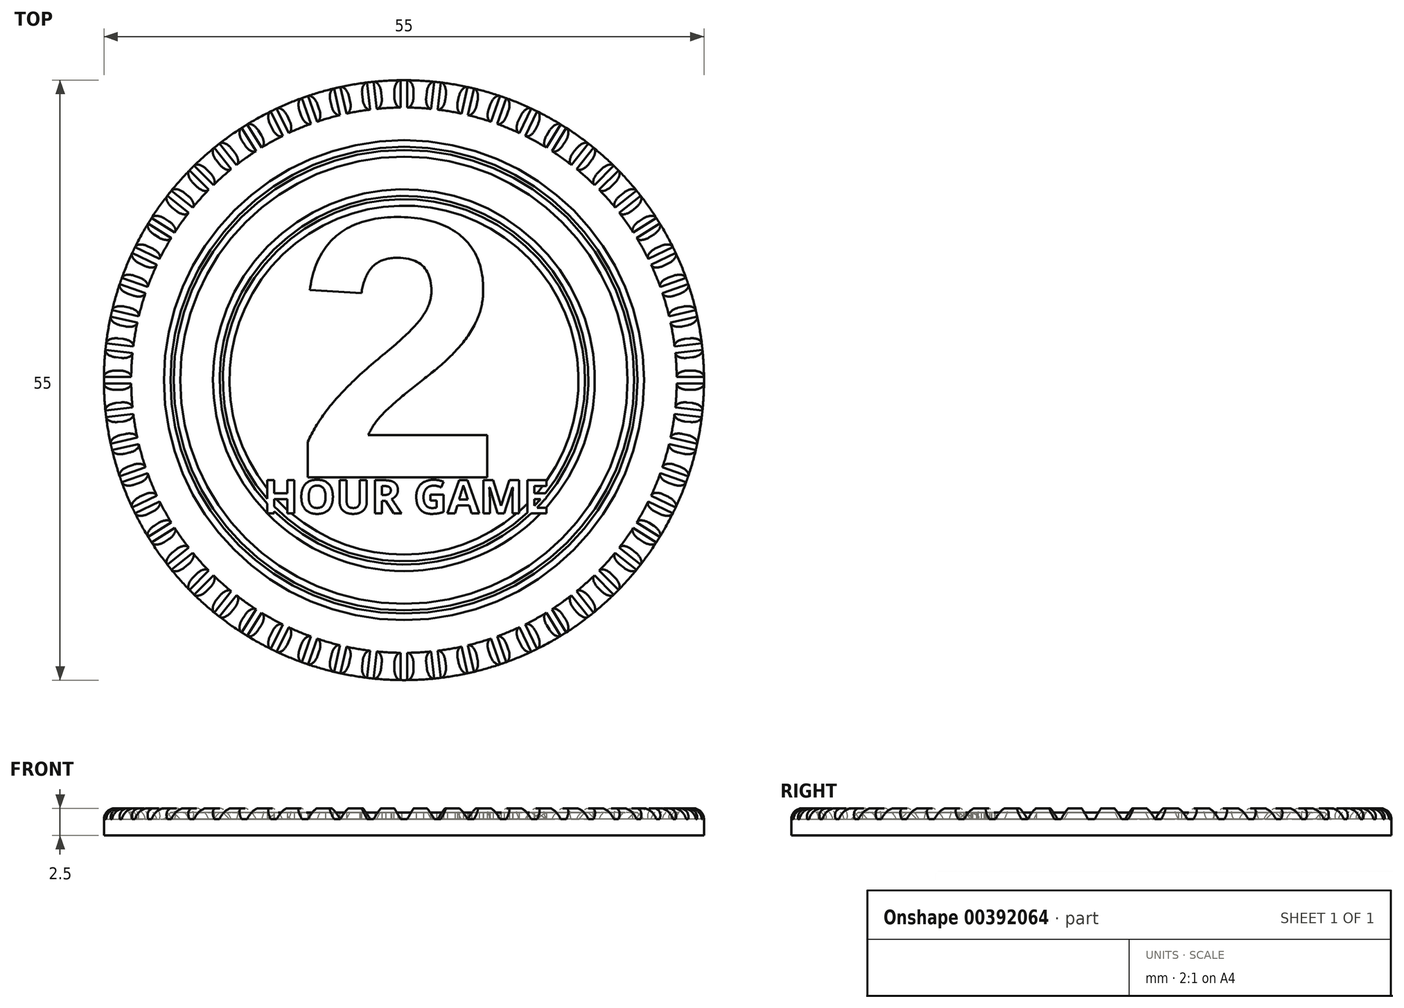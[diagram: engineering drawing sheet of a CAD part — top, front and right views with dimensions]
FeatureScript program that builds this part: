
annotation { "Feature Type Name" : "Feature", "Feature Type Description" : "" }
export const myFeature = defineFeature(function(context is Context, id is Id, definition is map)
    precondition{}
    {
        {
            var Q0;
            Q0=qCreatedBy(makeId("Top.planeOp"),FACE);
            var sketch = newSketch(context, id + "F0", { "sketchPlane" : qUnion([Q0])});
            skCircle(sketch, "E0", {"center": v(0, 0) * mm, "radius": 27.5 * mm});
            skSolve(sketch);
        }
        {
            var Q0;
            Q0=qSketchRegion(id+"F0",true);
            extrude(context, id + "F1", {"entities" : qUnion([Q0]), "depth" : 2.5 * mm});
        }
        {
            var Q0;
            Q0=makeQuery(id+"F1.opExtrude","CAP_FACE",FACE,{"disambiguationData":[OSD([sQuery(id+"F0.wireOp",EDGE,"E0")])],"isStart":false});
            var sketch = newSketch(context, id + "F2", { "sketchPlane" : qUnion([Q0])});
            skCircle(sketch, "E1.0", {"center": v(0, 0) * mm, "radius": 25 * mm});
            skSolve(sketch);
        }
        {
            var Q0;
            Q0=qSketchRegion(id+"F2",true);
            extrude(context, id + "F3", {"entities" : qUnion([Q0]), "operationType" : NewBodyOperationType.REMOVE, "oppositeDirection" : true, "depth" : 1 * mm});
        }
        {
            var Q0;
            Q0=makeQuery(id+"F1.opExtrude","CAP_FACE",FACE,{"disambiguationData":[OSD([sQuery(id+"F0.wireOp",EDGE,"E0")])],"isStart":false});
            fillet(context, id + "F4", {"entities" : qUnion([Q0]), "radius" : 1 * mm, "tangentPropagation" : true, "allowEdgeOverflow" : false});
        }
        {
            var Q0;
            Q0=qCreatedBy(makeId("Right.planeOp"),FACE);
            var sketch = newSketch(context, id + "F5", { "sketchPlane" : qUnion([Q0])});
            skLineSegment(sketch, "E2", {"start": v(0, 0) * mm, "end": v(0, 4.13) * mm, "construction": true});
            skLineSegment(sketch, "E3", {"start": v(0, 1.5) * mm, "end": v(-0.3, 1.5) * mm});
            skLineSegment(sketch, "E4", {"start": v(-0.3, 1.5) * mm, "end": v(-0.88, 2.5) * mm});
            skLineSegment(sketch, "E5", {"start": v(-0.88, 2.5) * mm, "end": v(0, 2.5) * mm});
            skLineSegment(sketch, "E6.MirrorCS", {"start": v(0, 1.5) * mm, "end": v(0.3, 1.5) * mm});
            skLineSegment(sketch, "E7.MirrorCS", {"start": v(0.88, 2.5) * mm, "end": v(0, 2.5) * mm});
            skLineSegment(sketch, "E8.MirrorCS", {"start": v(0.3, 1.5) * mm, "end": v(0.88, 2.5) * mm});
            skSolve(sketch);
        }
        {
            var Q0;
            Q0=qSketchRegion(id+"F5",true);
            extrude(context, id + "F6", {"entities" : qUnion([Q0]), "endBound" : BoundingType.THROUGH_ALL, "oppositeDirection" : true, "depth" : 25 * mm});
        }
        {
            var Q0;
            Q0=qCreatedBy(makeId("Front.planeOp"),FACE);
            var sketch = newSketch(context, id + "F7", { "sketchPlane" : qUnion([Q0])});
            skLineSegment(sketch, "E9", {"start": v(0, 0) * mm, "end": v(0, 9.54) * mm});
            skSolve(sketch);
        }
        {
            var Q0;
            Q0=makeQuery(id+"F6.opExtrude","SWEPT_BODY",BODY,{"disambiguationData":[OSD([sQuery(id+"F5.wireOp",EDGE,"E3"),sQuery(id+"F5.wireOp",EDGE,"E4"),sQuery(id+"F5.wireOp",EDGE,"E5"),sQuery(id+"F5.wireOp",EDGE,"E6.MirrorCS"),sQuery(id+"F5.wireOp",EDGE,"E7.MirrorCS"),sQuery(id+"F5.wireOp",EDGE,"E8.MirrorCS")])]});
            var Q1;
            Q1=sQuery(id+"F7.wireOp",EDGE,"E9");
            circularPattern(context, id + "F8", {"operationType" : NewBodyOperationType.REMOVE, "entities" : qUnion([Q0]), "axis" : qUnion([Q1]), "angle" : 360 * degree, "instanceCount" : 56, "equalSpace" : true, "computeTransformsWithoutBuiltin" : true});
        }
        {
            var Q0;
            {var subQ0=makeQuery(id+"F6.opExtrude","SWEPT_FACE",FACE,{"disambiguationData":[OSD([sQuery(id+"F5.wireOp",EDGE,"E3"),sQuery(id+"F5.wireOp",EDGE,"E6.MirrorCS")])]});Q0=makeQuery(id+"F8.boolean.opBoolean","MERGE",FACE,{"derivedFrom":[makeQuery(id+"F3.boolean.opBoolean","COPY",FACE,{"derivedFrom":makeQuery(id+"F3.opExtrude","CAP_FACE",FACE,{"disambiguationData":[OSD([sQuery(id+"F2.wireOp",EDGE,"E1.0")])],"isStart":false})}),subQ0,makeQuery(id+"F8.opPattern","COPY",FACE,{"derivedFrom":subQ0,"instanceName":"1"}),makeQuery(id+"F8.opPattern","COPY",FACE,{"derivedFrom":subQ0,"instanceName":"2"}),makeQuery(id+"F8.opPattern","COPY",FACE,{"derivedFrom":subQ0,"instanceName":"3"}),makeQuery(id+"F8.opPattern","COPY",FACE,{"derivedFrom":subQ0,"instanceName":"4"}),makeQuery(id+"F8.opPattern","COPY",FACE,{"derivedFrom":subQ0,"instanceName":"5"}),makeQuery(id+"F8.opPattern","COPY",FACE,{"derivedFrom":subQ0,"instanceName":"6"}),makeQuery(id+"F8.opPattern","COPY",FACE,{"derivedFrom":subQ0,"instanceName":"7"}),makeQuery(id+"F8.opPattern","COPY",FACE,{"derivedFrom":subQ0,"instanceName":"8"}),makeQuery(id+"F8.opPattern","COPY",FACE,{"derivedFrom":subQ0,"instanceName":"9"}),makeQuery(id+"F8.opPattern","COPY",FACE,{"derivedFrom":subQ0,"instanceName":"10"}),makeQuery(id+"F8.opPattern","COPY",FACE,{"derivedFrom":subQ0,"instanceName":"11"}),makeQuery(id+"F8.opPattern","COPY",FACE,{"derivedFrom":subQ0,"instanceName":"12"}),makeQuery(id+"F8.opPattern","COPY",FACE,{"derivedFrom":subQ0,"instanceName":"13"}),makeQuery(id+"F8.opPattern","COPY",FACE,{"derivedFrom":subQ0,"instanceName":"14"}),makeQuery(id+"F8.opPattern","COPY",FACE,{"derivedFrom":subQ0,"instanceName":"15"}),makeQuery(id+"F8.opPattern","COPY",FACE,{"derivedFrom":subQ0,"instanceName":"16"}),makeQuery(id+"F8.opPattern","COPY",FACE,{"derivedFrom":subQ0,"instanceName":"17"}),makeQuery(id+"F8.opPattern","COPY",FACE,{"derivedFrom":subQ0,"instanceName":"18"}),makeQuery(id+"F8.opPattern","COPY",FACE,{"derivedFrom":subQ0,"instanceName":"19"}),makeQuery(id+"F8.opPattern","COPY",FACE,{"derivedFrom":subQ0,"instanceName":"20"}),makeQuery(id+"F8.opPattern","COPY",FACE,{"derivedFrom":subQ0,"instanceName":"21"}),makeQuery(id+"F8.opPattern","COPY",FACE,{"derivedFrom":subQ0,"instanceName":"22"}),makeQuery(id+"F8.opPattern","COPY",FACE,{"derivedFrom":subQ0,"instanceName":"23"}),makeQuery(id+"F8.opPattern","COPY",FACE,{"derivedFrom":subQ0,"instanceName":"24"}),makeQuery(id+"F8.opPattern","COPY",FACE,{"derivedFrom":subQ0,"instanceName":"25"}),makeQuery(id+"F8.opPattern","COPY",FACE,{"derivedFrom":subQ0,"instanceName":"26"}),makeQuery(id+"F8.opPattern","COPY",FACE,{"derivedFrom":subQ0,"instanceName":"27"}),makeQuery(id+"F8.opPattern","COPY",FACE,{"derivedFrom":subQ0,"instanceName":"28"}),makeQuery(id+"F8.opPattern","COPY",FACE,{"derivedFrom":subQ0,"instanceName":"29"}),makeQuery(id+"F8.opPattern","COPY",FACE,{"derivedFrom":subQ0,"instanceName":"30"}),makeQuery(id+"F8.opPattern","COPY",FACE,{"derivedFrom":subQ0,"instanceName":"31"}),makeQuery(id+"F8.opPattern","COPY",FACE,{"derivedFrom":subQ0,"instanceName":"32"}),makeQuery(id+"F8.opPattern","COPY",FACE,{"derivedFrom":subQ0,"instanceName":"33"}),makeQuery(id+"F8.opPattern","COPY",FACE,{"derivedFrom":subQ0,"instanceName":"34"}),makeQuery(id+"F8.opPattern","COPY",FACE,{"derivedFrom":subQ0,"instanceName":"35"}),makeQuery(id+"F8.opPattern","COPY",FACE,{"derivedFrom":subQ0,"instanceName":"36"}),makeQuery(id+"F8.opPattern","COPY",FACE,{"derivedFrom":subQ0,"instanceName":"37"}),makeQuery(id+"F8.opPattern","COPY",FACE,{"derivedFrom":subQ0,"instanceName":"38"}),makeQuery(id+"F8.opPattern","COPY",FACE,{"derivedFrom":subQ0,"instanceName":"39"}),makeQuery(id+"F8.opPattern","COPY",FACE,{"derivedFrom":subQ0,"instanceName":"40"}),makeQuery(id+"F8.opPattern","COPY",FACE,{"derivedFrom":subQ0,"instanceName":"41"}),makeQuery(id+"F8.opPattern","COPY",FACE,{"derivedFrom":subQ0,"instanceName":"42"}),makeQuery(id+"F8.opPattern","COPY",FACE,{"derivedFrom":subQ0,"instanceName":"43"}),makeQuery(id+"F8.opPattern","COPY",FACE,{"derivedFrom":subQ0,"instanceName":"44"}),makeQuery(id+"F8.opPattern","COPY",FACE,{"derivedFrom":subQ0,"instanceName":"45"}),makeQuery(id+"F8.opPattern","COPY",FACE,{"derivedFrom":subQ0,"instanceName":"46"}),makeQuery(id+"F8.opPattern","COPY",FACE,{"derivedFrom":subQ0,"instanceName":"47"}),makeQuery(id+"F8.opPattern","COPY",FACE,{"derivedFrom":subQ0,"instanceName":"48"}),makeQuery(id+"F8.opPattern","COPY",FACE,{"derivedFrom":subQ0,"instanceName":"49"}),makeQuery(id+"F8.opPattern","COPY",FACE,{"derivedFrom":subQ0,"instanceName":"50"}),makeQuery(id+"F8.opPattern","COPY",FACE,{"derivedFrom":subQ0,"instanceName":"51"}),makeQuery(id+"F8.opPattern","COPY",FACE,{"derivedFrom":subQ0,"instanceName":"52"}),makeQuery(id+"F8.opPattern","COPY",FACE,{"derivedFrom":subQ0,"instanceName":"53"}),makeQuery(id+"F8.opPattern","COPY",FACE,{"derivedFrom":subQ0,"instanceName":"54"}),makeQuery(id+"F8.opPattern","COPY",FACE,{"derivedFrom":subQ0,"instanceName":"55"})]});}
            var sketch = newSketch(context, id + "F9", { "sketchPlane" : qUnion([Q0])});
            skText(sketch, "E10", { "text": "2", "fontName": "Arimo-Bold.ttf"});
            const initialGuessF9  = {"E10": [-0.01, -0.0089, 1, 0, 0.0246]};
            skSetInitialGuess(sketch, initialGuessF9);
            skSolve(sketch);
        }
        {
            var Q0;
            Q0=qSketchRegion(id+"F9",true);
            extrude(context, id + "F10", {"entities" : qUnion([Q0]), "operationType" : NewBodyOperationType.ADD, "depth" : 0.6 * mm});
        }
        {
            var Q0;
            {var subQ0=makeQuery(id+"F6.opExtrude","SWEPT_FACE",FACE,{"disambiguationData":[OSD([sQuery(id+"F5.wireOp",EDGE,"E3"),sQuery(id+"F5.wireOp",EDGE,"E6.MirrorCS")])]});Q0=makeQuery(id+"F8.boolean.opBoolean","MERGE",FACE,{"derivedFrom":[makeQuery(id+"F3.boolean.opBoolean","COPY",FACE,{"derivedFrom":makeQuery(id+"F3.opExtrude","CAP_FACE",FACE,{"disambiguationData":[OSD([sQuery(id+"F2.wireOp",EDGE,"E1.0")])],"isStart":false})}),subQ0,makeQuery(id+"F8.opPattern","COPY",FACE,{"derivedFrom":subQ0,"instanceName":"1"}),makeQuery(id+"F8.opPattern","COPY",FACE,{"derivedFrom":subQ0,"instanceName":"2"}),makeQuery(id+"F8.opPattern","COPY",FACE,{"derivedFrom":subQ0,"instanceName":"3"}),makeQuery(id+"F8.opPattern","COPY",FACE,{"derivedFrom":subQ0,"instanceName":"4"}),makeQuery(id+"F8.opPattern","COPY",FACE,{"derivedFrom":subQ0,"instanceName":"5"}),makeQuery(id+"F8.opPattern","COPY",FACE,{"derivedFrom":subQ0,"instanceName":"6"}),makeQuery(id+"F8.opPattern","COPY",FACE,{"derivedFrom":subQ0,"instanceName":"7"}),makeQuery(id+"F8.opPattern","COPY",FACE,{"derivedFrom":subQ0,"instanceName":"8"}),makeQuery(id+"F8.opPattern","COPY",FACE,{"derivedFrom":subQ0,"instanceName":"9"}),makeQuery(id+"F8.opPattern","COPY",FACE,{"derivedFrom":subQ0,"instanceName":"10"}),makeQuery(id+"F8.opPattern","COPY",FACE,{"derivedFrom":subQ0,"instanceName":"11"}),makeQuery(id+"F8.opPattern","COPY",FACE,{"derivedFrom":subQ0,"instanceName":"12"}),makeQuery(id+"F8.opPattern","COPY",FACE,{"derivedFrom":subQ0,"instanceName":"13"}),makeQuery(id+"F8.opPattern","COPY",FACE,{"derivedFrom":subQ0,"instanceName":"14"}),makeQuery(id+"F8.opPattern","COPY",FACE,{"derivedFrom":subQ0,"instanceName":"15"}),makeQuery(id+"F8.opPattern","COPY",FACE,{"derivedFrom":subQ0,"instanceName":"16"}),makeQuery(id+"F8.opPattern","COPY",FACE,{"derivedFrom":subQ0,"instanceName":"17"}),makeQuery(id+"F8.opPattern","COPY",FACE,{"derivedFrom":subQ0,"instanceName":"18"}),makeQuery(id+"F8.opPattern","COPY",FACE,{"derivedFrom":subQ0,"instanceName":"19"}),makeQuery(id+"F8.opPattern","COPY",FACE,{"derivedFrom":subQ0,"instanceName":"20"}),makeQuery(id+"F8.opPattern","COPY",FACE,{"derivedFrom":subQ0,"instanceName":"21"}),makeQuery(id+"F8.opPattern","COPY",FACE,{"derivedFrom":subQ0,"instanceName":"22"}),makeQuery(id+"F8.opPattern","COPY",FACE,{"derivedFrom":subQ0,"instanceName":"23"}),makeQuery(id+"F8.opPattern","COPY",FACE,{"derivedFrom":subQ0,"instanceName":"24"}),makeQuery(id+"F8.opPattern","COPY",FACE,{"derivedFrom":subQ0,"instanceName":"25"}),makeQuery(id+"F8.opPattern","COPY",FACE,{"derivedFrom":subQ0,"instanceName":"26"}),makeQuery(id+"F8.opPattern","COPY",FACE,{"derivedFrom":subQ0,"instanceName":"27"}),makeQuery(id+"F8.opPattern","COPY",FACE,{"derivedFrom":subQ0,"instanceName":"28"}),makeQuery(id+"F8.opPattern","COPY",FACE,{"derivedFrom":subQ0,"instanceName":"29"}),makeQuery(id+"F8.opPattern","COPY",FACE,{"derivedFrom":subQ0,"instanceName":"30"}),makeQuery(id+"F8.opPattern","COPY",FACE,{"derivedFrom":subQ0,"instanceName":"31"}),makeQuery(id+"F8.opPattern","COPY",FACE,{"derivedFrom":subQ0,"instanceName":"32"}),makeQuery(id+"F8.opPattern","COPY",FACE,{"derivedFrom":subQ0,"instanceName":"33"}),makeQuery(id+"F8.opPattern","COPY",FACE,{"derivedFrom":subQ0,"instanceName":"34"}),makeQuery(id+"F8.opPattern","COPY",FACE,{"derivedFrom":subQ0,"instanceName":"35"}),makeQuery(id+"F8.opPattern","COPY",FACE,{"derivedFrom":subQ0,"instanceName":"36"}),makeQuery(id+"F8.opPattern","COPY",FACE,{"derivedFrom":subQ0,"instanceName":"37"}),makeQuery(id+"F8.opPattern","COPY",FACE,{"derivedFrom":subQ0,"instanceName":"38"}),makeQuery(id+"F8.opPattern","COPY",FACE,{"derivedFrom":subQ0,"instanceName":"39"}),makeQuery(id+"F8.opPattern","COPY",FACE,{"derivedFrom":subQ0,"instanceName":"40"}),makeQuery(id+"F8.opPattern","COPY",FACE,{"derivedFrom":subQ0,"instanceName":"41"}),makeQuery(id+"F8.opPattern","COPY",FACE,{"derivedFrom":subQ0,"instanceName":"42"}),makeQuery(id+"F8.opPattern","COPY",FACE,{"derivedFrom":subQ0,"instanceName":"43"}),makeQuery(id+"F8.opPattern","COPY",FACE,{"derivedFrom":subQ0,"instanceName":"44"}),makeQuery(id+"F8.opPattern","COPY",FACE,{"derivedFrom":subQ0,"instanceName":"45"}),makeQuery(id+"F8.opPattern","COPY",FACE,{"derivedFrom":subQ0,"instanceName":"46"}),makeQuery(id+"F8.opPattern","COPY",FACE,{"derivedFrom":subQ0,"instanceName":"47"}),makeQuery(id+"F8.opPattern","COPY",FACE,{"derivedFrom":subQ0,"instanceName":"48"}),makeQuery(id+"F8.opPattern","COPY",FACE,{"derivedFrom":subQ0,"instanceName":"49"}),makeQuery(id+"F8.opPattern","COPY",FACE,{"derivedFrom":subQ0,"instanceName":"50"}),makeQuery(id+"F8.opPattern","COPY",FACE,{"derivedFrom":subQ0,"instanceName":"51"}),makeQuery(id+"F8.opPattern","COPY",FACE,{"derivedFrom":subQ0,"instanceName":"52"}),makeQuery(id+"F8.opPattern","COPY",FACE,{"derivedFrom":subQ0,"instanceName":"53"}),makeQuery(id+"F8.opPattern","COPY",FACE,{"derivedFrom":subQ0,"instanceName":"54"}),makeQuery(id+"F8.opPattern","COPY",FACE,{"derivedFrom":subQ0,"instanceName":"55"})]});}
            var sketch = newSketch(context, id + "F11", { "sketchPlane" : qUnion([Q0])});
            skText(sketch, "E11", { "text": "HOUR GAME", "fontName": "OpenSans-Bold.ttf"});
            const initialGuessF11  = {"E11": [-0.01292, -0.01222, 1, 0, 0.00307]};
            skSetInitialGuess(sketch, initialGuessF11);
            skSolve(sketch);
        }
        {
            var Q0;
            Q0=qSketchRegion(id+"F11",true);
            extrude(context, id + "F12", {"entities" : qUnion([Q0]), "operationType" : NewBodyOperationType.ADD, "depth" : 0.6 * mm});
        }
        {
            var Q0;
            {var subQ2=sQuery(id+"F0.wireOp",EDGE,"E0");var subQ3=sQuery(id+"F2.wireOp",EDGE,"E1.0");var subQ4=makeQuery(id+"F6.opExtrude","SWEPT_FACE",FACE,{"disambiguationData":[OSD([sQuery(id+"F5.wireOp",EDGE,"E3"),sQuery(id+"F5.wireOp",EDGE,"E6.MirrorCS")])]});Q0=makeQuery(id+"F12.boolean.opBoolean","SPLIT",FACE,{"disambiguationData":[TD([makeQuery(id+"F1.opExtrude","SWEPT_FACE",FACE,{"disambiguationData":[OSD([subQ2])]})])],"derivedFrom":makeQuery(id+"F8.boolean.opBoolean","MERGE",FACE,{"derivedFrom":[makeQuery(id+"F3.boolean.opBoolean","COPY",FACE,{"derivedFrom":makeQuery(id+"F3.opExtrude","CAP_FACE",FACE,{"disambiguationData":[OSD([subQ3])],"isStart":false})}),subQ4,makeQuery(id+"F8.opPattern","COPY",FACE,{"derivedFrom":subQ4,"instanceName":"1"}),makeQuery(id+"F8.opPattern","COPY",FACE,{"derivedFrom":subQ4,"instanceName":"2"}),makeQuery(id+"F8.opPattern","COPY",FACE,{"derivedFrom":subQ4,"instanceName":"3"}),makeQuery(id+"F8.opPattern","COPY",FACE,{"derivedFrom":subQ4,"instanceName":"4"}),makeQuery(id+"F8.opPattern","COPY",FACE,{"derivedFrom":subQ4,"instanceName":"5"}),makeQuery(id+"F8.opPattern","COPY",FACE,{"derivedFrom":subQ4,"instanceName":"6"}),makeQuery(id+"F8.opPattern","COPY",FACE,{"derivedFrom":subQ4,"instanceName":"7"}),makeQuery(id+"F8.opPattern","COPY",FACE,{"derivedFrom":subQ4,"instanceName":"8"}),makeQuery(id+"F8.opPattern","COPY",FACE,{"derivedFrom":subQ4,"instanceName":"9"}),makeQuery(id+"F8.opPattern","COPY",FACE,{"derivedFrom":subQ4,"instanceName":"10"}),makeQuery(id+"F8.opPattern","COPY",FACE,{"derivedFrom":subQ4,"instanceName":"11"}),makeQuery(id+"F8.opPattern","COPY",FACE,{"derivedFrom":subQ4,"instanceName":"12"}),makeQuery(id+"F8.opPattern","COPY",FACE,{"derivedFrom":subQ4,"instanceName":"13"}),makeQuery(id+"F8.opPattern","COPY",FACE,{"derivedFrom":subQ4,"instanceName":"14"}),makeQuery(id+"F8.opPattern","COPY",FACE,{"derivedFrom":subQ4,"instanceName":"15"}),makeQuery(id+"F8.opPattern","COPY",FACE,{"derivedFrom":subQ4,"instanceName":"16"}),makeQuery(id+"F8.opPattern","COPY",FACE,{"derivedFrom":subQ4,"instanceName":"17"}),makeQuery(id+"F8.opPattern","COPY",FACE,{"derivedFrom":subQ4,"instanceName":"18"}),makeQuery(id+"F8.opPattern","COPY",FACE,{"derivedFrom":subQ4,"instanceName":"19"}),makeQuery(id+"F8.opPattern","COPY",FACE,{"derivedFrom":subQ4,"instanceName":"20"}),makeQuery(id+"F8.opPattern","COPY",FACE,{"derivedFrom":subQ4,"instanceName":"21"}),makeQuery(id+"F8.opPattern","COPY",FACE,{"derivedFrom":subQ4,"instanceName":"22"}),makeQuery(id+"F8.opPattern","COPY",FACE,{"derivedFrom":subQ4,"instanceName":"23"}),makeQuery(id+"F8.opPattern","COPY",FACE,{"derivedFrom":subQ4,"instanceName":"24"}),makeQuery(id+"F8.opPattern","COPY",FACE,{"derivedFrom":subQ4,"instanceName":"25"}),makeQuery(id+"F8.opPattern","COPY",FACE,{"derivedFrom":subQ4,"instanceName":"26"}),makeQuery(id+"F8.opPattern","COPY",FACE,{"derivedFrom":subQ4,"instanceName":"27"}),makeQuery(id+"F8.opPattern","COPY",FACE,{"derivedFrom":subQ4,"instanceName":"28"}),makeQuery(id+"F8.opPattern","COPY",FACE,{"derivedFrom":subQ4,"instanceName":"29"}),makeQuery(id+"F8.opPattern","COPY",FACE,{"derivedFrom":subQ4,"instanceName":"30"}),makeQuery(id+"F8.opPattern","COPY",FACE,{"derivedFrom":subQ4,"instanceName":"31"}),makeQuery(id+"F8.opPattern","COPY",FACE,{"derivedFrom":subQ4,"instanceName":"32"}),makeQuery(id+"F8.opPattern","COPY",FACE,{"derivedFrom":subQ4,"instanceName":"33"}),makeQuery(id+"F8.opPattern","COPY",FACE,{"derivedFrom":subQ4,"instanceName":"34"}),makeQuery(id+"F8.opPattern","COPY",FACE,{"derivedFrom":subQ4,"instanceName":"35"}),makeQuery(id+"F8.opPattern","COPY",FACE,{"derivedFrom":subQ4,"instanceName":"36"}),makeQuery(id+"F8.opPattern","COPY",FACE,{"derivedFrom":subQ4,"instanceName":"37"}),makeQuery(id+"F8.opPattern","COPY",FACE,{"derivedFrom":subQ4,"instanceName":"38"}),makeQuery(id+"F8.opPattern","COPY",FACE,{"derivedFrom":subQ4,"instanceName":"39"}),makeQuery(id+"F8.opPattern","COPY",FACE,{"derivedFrom":subQ4,"instanceName":"40"}),makeQuery(id+"F8.opPattern","COPY",FACE,{"derivedFrom":subQ4,"instanceName":"41"}),makeQuery(id+"F8.opPattern","COPY",FACE,{"derivedFrom":subQ4,"instanceName":"42"}),makeQuery(id+"F8.opPattern","COPY",FACE,{"derivedFrom":subQ4,"instanceName":"43"}),makeQuery(id+"F8.opPattern","COPY",FACE,{"derivedFrom":subQ4,"instanceName":"44"}),makeQuery(id+"F8.opPattern","COPY",FACE,{"derivedFrom":subQ4,"instanceName":"45"}),makeQuery(id+"F8.opPattern","COPY",FACE,{"derivedFrom":subQ4,"instanceName":"46"}),makeQuery(id+"F8.opPattern","COPY",FACE,{"derivedFrom":subQ4,"instanceName":"47"}),makeQuery(id+"F8.opPattern","COPY",FACE,{"derivedFrom":subQ4,"instanceName":"48"}),makeQuery(id+"F8.opPattern","COPY",FACE,{"derivedFrom":subQ4,"instanceName":"49"}),makeQuery(id+"F8.opPattern","COPY",FACE,{"derivedFrom":subQ4,"instanceName":"50"}),makeQuery(id+"F8.opPattern","COPY",FACE,{"derivedFrom":subQ4,"instanceName":"51"}),makeQuery(id+"F8.opPattern","COPY",FACE,{"derivedFrom":subQ4,"instanceName":"52"}),makeQuery(id+"F8.opPattern","COPY",FACE,{"derivedFrom":subQ4,"instanceName":"53"}),makeQuery(id+"F8.opPattern","COPY",FACE,{"derivedFrom":subQ4,"instanceName":"54"}),makeQuery(id+"F8.opPattern","COPY",FACE,{"derivedFrom":subQ4,"instanceName":"55"})]})});}
            var sketch = newSketch(context, id + "F13", { "sketchPlane" : qUnion([Q0])});
            skCircle(sketch, "E12", {"center": v(0, 0) * mm, "radius": 16 * mm});
            skCircle(sketch, "E13.0", {"center": v(0, 0) * mm, "radius": 17.5 * mm});
            skSolve(sketch);
        }
        {
            var Q0;
            Q0 = qSketchRegion(id + "F13", true);
            extrude(context, id + "F14", {"entities" : qUnion([Q0]), "operationType" : NewBodyOperationType.ADD, "depth" : 0.6 * mm, "hasDraft" : true, "draftAngle" : 45 * degree, "draftPullDirection" : true});
        }
        {
            var Q0;
            {var subQ71=sQuery(id+"F0.wireOp",EDGE,"E0");var subQ76=sQuery(id+"F2.wireOp",EDGE,"E1.0");var subQ96=makeQuery(id+"F1.opExtrude","SWEPT_FACE",FACE,{"disambiguationData":[OSD([subQ71])]});var subQ140=makeQuery(id+"F6.opExtrude","SWEPT_FACE",FACE,{"disambiguationData":[OSD([sQuery(id+"F5.wireOp",EDGE,"E3"),sQuery(id+"F5.wireOp",EDGE,"E6.MirrorCS")])]});Q0=makeQuery(id+"F14.boolean.opBoolean","SPLIT",FACE,{"disambiguationData":[TD([subQ96])],"derivedFrom":makeQuery(id+"F12.boolean.opBoolean","SPLIT",FACE,{"disambiguationData":[TD([subQ96])],"derivedFrom":makeQuery(id+"F8.boolean.opBoolean","MERGE",FACE,{"derivedFrom":[makeQuery(id+"F3.boolean.opBoolean","COPY",FACE,{"derivedFrom":makeQuery(id+"F3.opExtrude","CAP_FACE",FACE,{"disambiguationData":[OSD([subQ76])],"isStart":false})}),subQ140,makeQuery(id+"F8.opPattern","COPY",FACE,{"derivedFrom":subQ140,"instanceName":"1"}),makeQuery(id+"F8.opPattern","COPY",FACE,{"derivedFrom":subQ140,"instanceName":"2"}),makeQuery(id+"F8.opPattern","COPY",FACE,{"derivedFrom":subQ140,"instanceName":"3"}),makeQuery(id+"F8.opPattern","COPY",FACE,{"derivedFrom":subQ140,"instanceName":"4"}),makeQuery(id+"F8.opPattern","COPY",FACE,{"derivedFrom":subQ140,"instanceName":"5"}),makeQuery(id+"F8.opPattern","COPY",FACE,{"derivedFrom":subQ140,"instanceName":"6"}),makeQuery(id+"F8.opPattern","COPY",FACE,{"derivedFrom":subQ140,"instanceName":"7"}),makeQuery(id+"F8.opPattern","COPY",FACE,{"derivedFrom":subQ140,"instanceName":"8"}),makeQuery(id+"F8.opPattern","COPY",FACE,{"derivedFrom":subQ140,"instanceName":"9"}),makeQuery(id+"F8.opPattern","COPY",FACE,{"derivedFrom":subQ140,"instanceName":"10"}),makeQuery(id+"F8.opPattern","COPY",FACE,{"derivedFrom":subQ140,"instanceName":"11"}),makeQuery(id+"F8.opPattern","COPY",FACE,{"derivedFrom":subQ140,"instanceName":"12"}),makeQuery(id+"F8.opPattern","COPY",FACE,{"derivedFrom":subQ140,"instanceName":"13"}),makeQuery(id+"F8.opPattern","COPY",FACE,{"derivedFrom":subQ140,"instanceName":"14"}),makeQuery(id+"F8.opPattern","COPY",FACE,{"derivedFrom":subQ140,"instanceName":"15"}),makeQuery(id+"F8.opPattern","COPY",FACE,{"derivedFrom":subQ140,"instanceName":"16"}),makeQuery(id+"F8.opPattern","COPY",FACE,{"derivedFrom":subQ140,"instanceName":"17"}),makeQuery(id+"F8.opPattern","COPY",FACE,{"derivedFrom":subQ140,"instanceName":"18"}),makeQuery(id+"F8.opPattern","COPY",FACE,{"derivedFrom":subQ140,"instanceName":"19"}),makeQuery(id+"F8.opPattern","COPY",FACE,{"derivedFrom":subQ140,"instanceName":"20"}),makeQuery(id+"F8.opPattern","COPY",FACE,{"derivedFrom":subQ140,"instanceName":"21"}),makeQuery(id+"F8.opPattern","COPY",FACE,{"derivedFrom":subQ140,"instanceName":"22"}),makeQuery(id+"F8.opPattern","COPY",FACE,{"derivedFrom":subQ140,"instanceName":"23"}),makeQuery(id+"F8.opPattern","COPY",FACE,{"derivedFrom":subQ140,"instanceName":"24"}),makeQuery(id+"F8.opPattern","COPY",FACE,{"derivedFrom":subQ140,"instanceName":"25"}),makeQuery(id+"F8.opPattern","COPY",FACE,{"derivedFrom":subQ140,"instanceName":"26"}),makeQuery(id+"F8.opPattern","COPY",FACE,{"derivedFrom":subQ140,"instanceName":"27"}),makeQuery(id+"F8.opPattern","COPY",FACE,{"derivedFrom":subQ140,"instanceName":"28"}),makeQuery(id+"F8.opPattern","COPY",FACE,{"derivedFrom":subQ140,"instanceName":"29"}),makeQuery(id+"F8.opPattern","COPY",FACE,{"derivedFrom":subQ140,"instanceName":"30"}),makeQuery(id+"F8.opPattern","COPY",FACE,{"derivedFrom":subQ140,"instanceName":"31"}),makeQuery(id+"F8.opPattern","COPY",FACE,{"derivedFrom":subQ140,"instanceName":"32"}),makeQuery(id+"F8.opPattern","COPY",FACE,{"derivedFrom":subQ140,"instanceName":"33"}),makeQuery(id+"F8.opPattern","COPY",FACE,{"derivedFrom":subQ140,"instanceName":"34"}),makeQuery(id+"F8.opPattern","COPY",FACE,{"derivedFrom":subQ140,"instanceName":"35"}),makeQuery(id+"F8.opPattern","COPY",FACE,{"derivedFrom":subQ140,"instanceName":"36"}),makeQuery(id+"F8.opPattern","COPY",FACE,{"derivedFrom":subQ140,"instanceName":"37"}),makeQuery(id+"F8.opPattern","COPY",FACE,{"derivedFrom":subQ140,"instanceName":"38"}),makeQuery(id+"F8.opPattern","COPY",FACE,{"derivedFrom":subQ140,"instanceName":"39"}),makeQuery(id+"F8.opPattern","COPY",FACE,{"derivedFrom":subQ140,"instanceName":"40"}),makeQuery(id+"F8.opPattern","COPY",FACE,{"derivedFrom":subQ140,"instanceName":"41"}),makeQuery(id+"F8.opPattern","COPY",FACE,{"derivedFrom":subQ140,"instanceName":"42"}),makeQuery(id+"F8.opPattern","COPY",FACE,{"derivedFrom":subQ140,"instanceName":"43"}),makeQuery(id+"F8.opPattern","COPY",FACE,{"derivedFrom":subQ140,"instanceName":"44"}),makeQuery(id+"F8.opPattern","COPY",FACE,{"derivedFrom":subQ140,"instanceName":"45"}),makeQuery(id+"F8.opPattern","COPY",FACE,{"derivedFrom":subQ140,"instanceName":"46"}),makeQuery(id+"F8.opPattern","COPY",FACE,{"derivedFrom":subQ140,"instanceName":"47"}),makeQuery(id+"F8.opPattern","COPY",FACE,{"derivedFrom":subQ140,"instanceName":"48"}),makeQuery(id+"F8.opPattern","COPY",FACE,{"derivedFrom":subQ140,"instanceName":"49"}),makeQuery(id+"F8.opPattern","COPY",FACE,{"derivedFrom":subQ140,"instanceName":"50"}),makeQuery(id+"F8.opPattern","COPY",FACE,{"derivedFrom":subQ140,"instanceName":"51"}),makeQuery(id+"F8.opPattern","COPY",FACE,{"derivedFrom":subQ140,"instanceName":"52"}),makeQuery(id+"F8.opPattern","COPY",FACE,{"derivedFrom":subQ140,"instanceName":"53"}),makeQuery(id+"F8.opPattern","COPY",FACE,{"derivedFrom":subQ140,"instanceName":"54"}),makeQuery(id+"F8.opPattern","COPY",FACE,{"derivedFrom":subQ140,"instanceName":"55"})]})})});}
            var sketch = newSketch(context, id + "F15", { "sketchPlane" : qUnion([Q0])});
            skCircle(sketch, "E14", {"center": v(0, 0) * mm, "radius": 20.5 * mm});
            skCircle(sketch, "E15.0", {"center": v(0, 0) * mm, "radius": 22 * mm});
            skSolve(sketch);
        }
        {
            var Q0;
            Q0 = qSketchRegion(id + "F15", true);
            extrude(context, id + "F16", {"entities" : qUnion([Q0]), "operationType" : NewBodyOperationType.ADD, "depth" : 0.6 * mm, "hasDraft" : true, "draftAngle" : 45 * degree, "draftPullDirection" : true});
        }
    });
